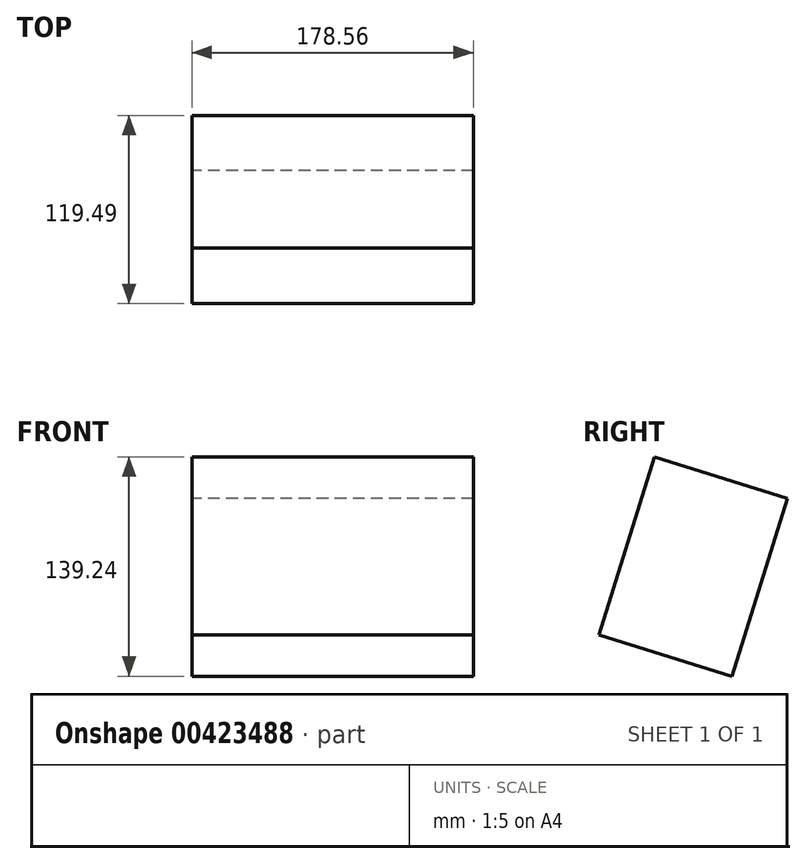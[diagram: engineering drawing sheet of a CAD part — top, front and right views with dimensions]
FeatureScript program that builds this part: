
annotation { "Feature Type Name" : "Feature", "Feature Type Description" : "" }
export const myFeature = defineFeature(function(context is Context, id is Id, definition is map)
    precondition{}
    {
        {
            var Q0;
            Q0=qCreatedBy(makeId("Right.planeOp"),FACE);
            var sketch = newSketch(context, id + "F0", { "sketchPlane" : qUnion([Q0])});
            skLineSegment(sketch, "E0", {"start": v(-52.35, 34.06) * mm, "end": v(36.57, -50.35) * mm});
            skLineSegment(sketch, "E1", {"start": v(36.57, -50.35) * mm, "end": v(-47.79, -24.14) * mm});
            skSolve(sketch);
        }
        {
            var Q0;
            Q0=sQuery(id+"F0.wireOp",EDGE,"E1");
            extrude(context, id + "F1", {"bodyType" : ToolBodyType.SURFACE, "surfaceEntities" : qUnion([Q0]), "oppositeDirection" : true, "depth" : 178.56 * mm});
        }
        {
            var Q0;
            Q0=makeQuery(id+"F1.opExtrude","SWEPT_FACE",FACE,{"disambiguationData":[OSD([sQuery(id+"F0.wireOp",EDGE,"E1")])]});
            extrude(context, id + "F2", {"entities" : qUnion([Q0]), "oppositeDirection" : true, "depth" : 118.36 * mm});
        }
    });
